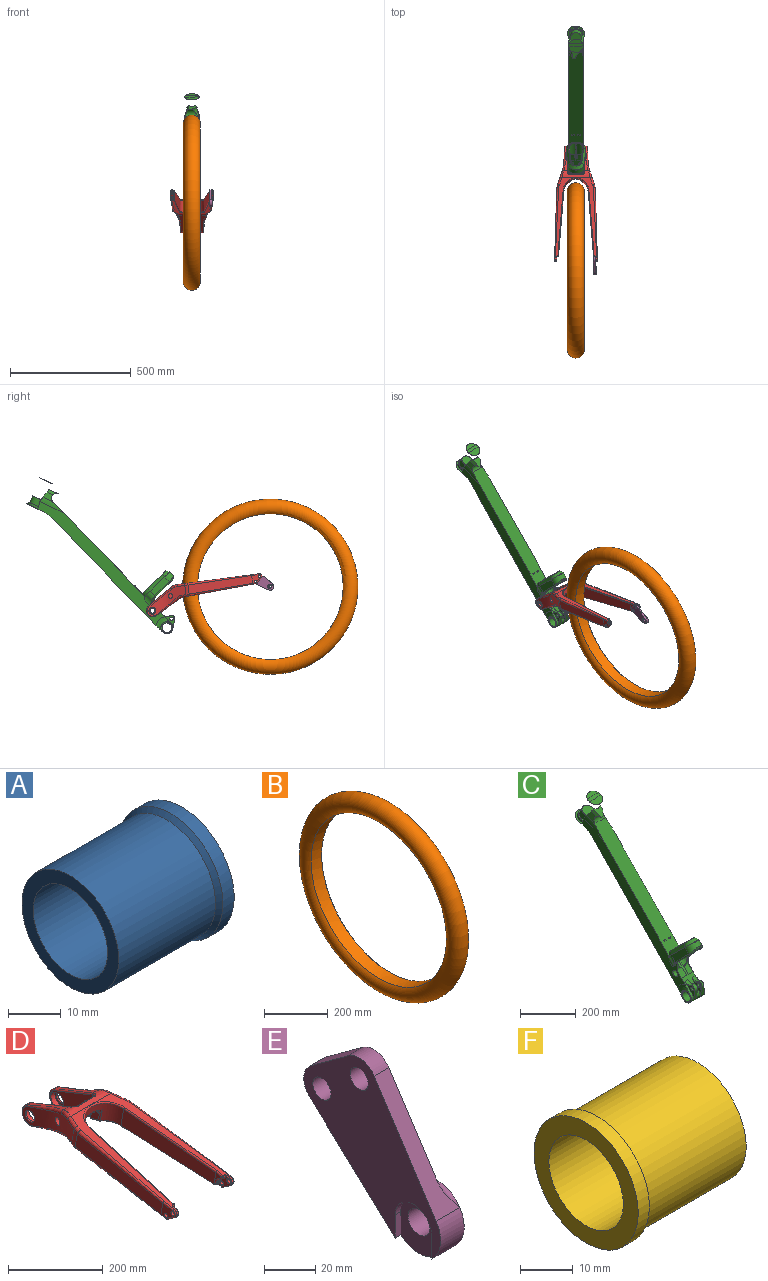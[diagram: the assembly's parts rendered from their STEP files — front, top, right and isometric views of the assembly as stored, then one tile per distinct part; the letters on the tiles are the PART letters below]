
ASSEMBLY  parts=6 mates=7
PART A: 6 faces, bbox 30x28x28 mm
  f0: cylinder r=13mm len=26mm, axis (-1,0,0), area 2123.7mm2, adj f3,f5
  f1: cylinder r=10mm len=30mm, axis (-1,0,0), area 1885mm2, adj f2,f3
  f2: plane 28x28mm, normal (1,0,0), area 301.6mm2, adj f1,f4
  f3: plane 26x26mm, normal (-1,0,0), area 216.8mm2, adj f0,f1
  f4: cylinder r=14mm len=28mm, axis (1,0,0), area 263.9mm2, adj f2,f5
  f5: cone r=14mm half-angle=45deg, axis (1,0,0), area 120mm2, adj f0,f4
PART B: 2 faces, bbox 47.1x784.7x784.7 mm
  f0: torus R=327.5mm, axis (-1,0,0), area 356678mm2, adj f1
  f1: cylinder r=301.59mm len=603.18mm, axis (1,0,0), area 89169.2mm2, adj f0
PART C: 127 faces, bbox 114.2x654.6x672 mm
  f0: cylinder r=14mm len=20.9mm, axis (-1,0,0), area 450.7mm2, adj f1,f2,f45,f63
  f1: plane 39.93x14mm, normal (0,-0.98,-0.21), area 572mm2, adj f0,f31,f45,f63
  f2: cylinder r=25mm len=30.24mm, axis (-1,0,0), area 460.2mm2, adj f0,f6,f45,f63
  f3: plane 13.6x6.41mm, normal (0,-0.9,-0.43), area 46.5mm2, adj f34,f53,f88,f90
  f4: cylinder r=27.5mm len=82.26mm, axis (0,0.7,0.72), area 2320.4mm2, adj f6,f18,f48,f105,f106,f108,f109
  f5: cylinder r=27.5mm len=93.75mm, axis (0,0.7,0.72), area 2418.2mm2, adj f6,f17,f52,f53,f56
  f6: plane 518.11x504.25mm, normal (0,-0.72,0.7), area 34991.8mm2, adj f2,f4,f5,f20,f22,f26,f31,f34
  f7: cylinder r=40.63mm len=44.38mm, axis (0,0.7,0.72), area 639mm2, adj f8,f26,f34,f88
  f8: cylinder r=40.5mm len=40.95mm, axis (0,0.7,0.72), area 751.8mm2, adj f7,f16,f26,f90,f92
  f9: cylinder r=40.63mm len=44.38mm, axis (0,0.7,0.72), area 639mm2, adj f10,f22,f35,f83
  f10: cylinder r=40.5mm len=40.95mm, axis (0,0.7,0.72), area 756.9mm2, adj f9,f19,f22,f87,f89,f91
  f11: cylinder r=14mm len=20.9mm, axis (-1,0,0), area 264.5mm2, adj f12,f57,f117,f118,f119,f125
  f12: plane 39.94x20.13mm, normal (0,-0.98,-0.21), area 591.2mm2, adj f11,f31,f115,f116,f124
  f13: cylinder r=19.5mm len=41.35mm, axis (0,0.7,0.72), area 2252mm2, adj f17,f18,f50,f100,f101,f102
  f14: cylinder r=32.5mm len=64.71mm, axis (0,0.7,0.72), area 2404.8mm2, adj f16,f19,f24,f69,f70,f97,f98,f99
  f15: plane 62.39x60.67mm, normal (0,-0.7,-0.72), area 665.4mm2, adj f17,f43,f53,f96,f98,f100
  f16: plane 79.78x78.67mm, normal (-1,-0.07,0.07), area 2352.5mm2, adj f8,f14,f25,f94,f96
  f17: plane 90.62x89.31mm, normal (1,0.07,-0.07), area 3668.3mm2, adj f5,f13,f15,f51,f53,f100
  f18: plane 88.63x87.78mm, normal (-1,0.07,-0.07), area 3427.2mm2, adj f4,f13,f49,f103,f104
  f19: plane 79.78x78.67mm, normal (1,-0.07,0.07), area 2352.5mm2, adj f10,f14,f23,f93,f95
  f20: plane 97.72x95.03mm, normal (0,0.7,0.72), area 490.3mm2, adj f6,f22,f23,f24,f25,f26,f48,f49
  f21: plane 62.39x60.67mm, normal (0,-0.7,-0.72), area 437.2mm2, adj f43,f54,f95,f97,f102,f103
  f22: bspline ~57.03x46.15mm, area 649.6mm2, adj f6,f9,f10,f20,f23,f35
  f23: bspline ~70.52x68mm, area 1360.7mm2, adj f19,f20,f22,f24
  f24: cone r=24.08mm half-angle=31.6deg, axis (0,-0.7,-0.72), area 1343.4mm2, adj f14,f20,f23,f25,f70
  f25: plane 70.52x68mm, normal (-0.85,0.31,0.43), area 1360.7mm2, adj f16,f20,f24,f26
  f26: cone r=32.08mm half-angle=31.6deg, axis (0,-0.7,-0.72), area 649.6mm2, adj f6,f7,f8,f20,f25,f34
  f27: plane 486.45x473.46mm, normal (0,0.72,-0.7), area 39699.1mm2, adj f31,f34,f35,f42,f46,f47
  f28: plane 70x63.93mm, normal (0,0.42,-0.91), area 1759.2mm2, adj f30,f34,f35,f42,f72
  f29: plane 60x54.38mm, normal (0,-0.42,0.91), area 2827.4mm2, adj f30
  f30: cone r=35mm half-angle=2.4deg, axis (0,0.42,-0.91), area 18673.1mm2, adj f28,f29,f34,f35,f36,f38,f39,f40
  f31: cylinder r=25mm len=68mm, axis (-1,0,0), area 4406.2mm2, adj f1,f6,f12,f27,f32,f33,f45,f63
  f32: plane 52.23x52.17mm, normal (1,0,0), area 703.6mm2, adj f31,f47,f59,f71,f115,f123
  f33: plane 50.04x50.04mm, normal (-1,0,0), area 706.9mm2, adj f31,f46,f71
  f34: plane 533.49x518.73mm, normal (-1,0,0), area 32458.6mm2, adj f3,f6,f7,f26,f27,f28,f30,f42
  f35: plane 532.73x520.81mm, normal (1,0,0), area 32191.3mm2, adj f6,f9,f22,f27,f28,f30,f40,f42
  f36: plane 38.13x32mm, normal (0,-0.42,0.91), area 954.4mm2, adj f30,f37,f38,f41,f44
  f37: cylinder r=20mm len=54.09mm, axis (-1,0,0), area 1926.3mm2, adj f6,f36,f41,f44,f80
  f38: plane 22.15x15.87mm, normal (0.91,-0.18,0.38), area 185.7mm2, adj f30,f36,f39,f44
  f39: plane 49.21x48.35mm, normal (0.98,-0.09,0.2), area 773.4mm2, adj f6,f30,f38,f40,f44
  f40: cylinder r=80mm len=97.39mm, axis (0,0.91,0.42), area 1320.5mm2, adj f6,f30,f35,f39
  f41: plane 48.89x23.35mm, normal (-0.91,-0.18,0.38), area 400.2mm2, adj f30,f36,f37,f80
  f42: bspline ~66x41.2mm, area 3061.4mm2, adj f27,f28,f34,f35
  f43: cylinder r=50mm len=53.79mm, axis (1,0,0), area 418.9mm2, adj f15,f21,f99,f101
  f44: bspline ~56.72x48.38mm, area 611.3mm2, adj f6,f36,f37,f38,f39
  f45: plane 59.4x51.14mm, normal (-1,0,0), area 840mm2, adj f0,f1,f2,f6,f31,f66
  f46: bspline ~84.75x83.82mm, area 1590.5mm2, adj f6,f27,f33,f34
  f47: bspline ~81.68x80.82mm, area 1515mm2, adj f27,f32,f35,f123
  f48: torus R=30.5mm, axis (0,0.7,0.72), area 182.5mm2, adj f4,f6,f20,f49
  f49: cylinder r=3mm len=62.3mm, axis (0.09,0.71,-0.69), area 398.8mm2, adj f18,f20,f48,f50
  f50: torus R=22.5mm, axis (0,0.7,0.72), area 286.5mm2, adj f13,f20,f49,f51
  f51: cylinder r=3mm len=62.3mm, axis (0.09,-0.71,0.69), area 398.8mm2, adj f17,f20,f50,f52
  f52: torus R=30.5mm, axis (0,0.7,0.72), area 182.5mm2, adj f5,f6,f20,f51
  f53: cylinder r=20mm len=8.23mm, axis (1,0,0), area 57.2mm2, adj f3,f5,f15,f17,f56,f92,f94
  f54: cylinder r=20mm len=5.6mm, axis (1,0,0), area 30.6mm2, adj f21,f86,f91,f93,f104,f106,f108
  f55: bspline ~57.54x28.6mm, area 859.5mm2, adj f6,f60,f105
  f56: bspline ~57.54x28.6mm, area 1118.3mm2, adj f5,f6,f34,f53
  f57: cylinder r=25mm len=30.24mm, axis (-1,0,0), area 408.3mm2, adj f6,f11,f62,f120,f126
  f58: bspline ~52.19x48.46mm, area 447.7mm2, adj f59,f112,f116,f117,f118,f119,f120,f122
  f59: torus R=53.89mm, axis (1,0,0), area 126.3mm2, adj f32,f58,f115,f123
  f60: bspline ~89.08x62.35mm, area 237.3mm2, adj f35,f55,f61,f85,f107
  f61: cylinder r=3mm len=13.08mm, axis (0,-0.7,-0.72), area 72.2mm2, adj f6,f35,f60,f62
  f62: torus R=28mm, axis (1,0,0), area 48.8mm2, adj f35,f57,f61,f121
  f63: plane 59.4x51.14mm, normal (1,0,0), area 840mm2, adj f0,f1,f2,f6,f31,f66
  f64: plane 41.65x39.35mm, normal (-1,0,0), area 576.3mm2, adj f6,f31,f65,f124,f125,f126
  f65: cylinder r=7mm len=14mm, axis (1,0,0), area 439.8mm2, adj f64,f113
  f66: cylinder r=7mm len=14mm, axis (1,0,0), area 615.8mm2, adj f45,f63
  f67: cylinder r=10mm len=7mm, axis (1,0,0), area 37.2mm2, adj f6,f77,f78,f111
  f68: cylinder r=10mm len=7mm, axis (1,0,0), area 37.2mm2, adj f6,f76,f79,f110
  f69: plane 7.62x1.13mm, normal (0,-0.26,0.97), area 2.4mm2, adj f14,f70
  f70: bspline ~13.36x2.85mm, area 28.4mm2, adj f14,f24,f69
  f71: cylinder r=20mm len=68mm, axis (1,0,0), area 8545.1mm2, adj f32,f33
  f72: cylinder r=27.75mm len=55.5mm, axis (0,0.42,-0.91), area 1743.6mm2, adj f28,f73
  f73: plane 55.5x50.3mm, normal (0,0.42,-0.91), area 757.3mm2, adj f72,f74
  f74: cylinder r=23mm len=54.37mm, axis (0,0.42,-0.91), area 4335.4mm2, adj f73,f75
  f75: plane 46x41.69mm, normal (0,0.42,-0.91), area 1661.9mm2, adj f74
  f76: torus R=12mm, axis (1,0,0), area 7mm2, adj f6,f68,f110
  f77: torus R=12mm, axis (1,0,0), area 7mm2, adj f6,f67,f111
  f78: torus R=12mm, axis (1,0,0), area 7mm2, adj f6,f67,f111
  f79: torus R=12mm, axis (1,0,0), area 7mm2, adj f6,f68,f110
  f80: plane 43.64x43.2mm, normal (-0.98,-0.09,0.2), area 870mm2, adj f6,f30,f37,f41,f81
  f81: cylinder r=100mm len=104.27mm, axis (0,0.91,0.42), area 1643.5mm2, adj f6,f30,f34,f80
  f82: cylinder r=13mm len=59mm, axis (1,0,0), area 4819.2mm2, adj f34,f114
  f83: bspline ~25.89x16.45mm, area 38.8mm2, adj f9,f84,f85,f87
  f84: bspline ~23.63x22.58mm, area 82.8mm2, adj f35,f83,f85
  f85: bspline ~24.54x10.4mm, area 114.3mm2, adj f60,f83,f84,f86,f87,f109
  f86: bspline ~14.83x11.3mm, area 36.8mm2, adj f54,f85,f89,f108
  f87: bspline ~10.79x9.47mm, area 44.9mm2, adj f10,f83,f85,f89
  f88: bspline ~22.11x14.75mm, area 104.7mm2, adj f3,f7,f34,f90
  f89: bspline ~13.75x9.79mm, area 50.7mm2, adj f10,f86,f87,f91
  f90: bspline ~20.07x13.73mm, area 127.4mm2, adj f3,f8,f88,f92
  f91: bspline ~12.99x11.67mm, area 63.4mm2, adj f10,f54,f89,f93
  f92: bspline ~12.99x11.67mm, area 65.4mm2, adj f8,f53,f90,f94
  f93: bspline ~9.31x9.09mm, area 2.5mm2, adj f19,f54,f91,f95
  f94: bspline ~9.31x9.09mm, area 2.5mm2, adj f16,f53,f92,f96
  f95: cylinder r=5mm len=63.3mm, axis (0.09,0.71,-0.69), area 661.7mm2, adj f19,f21,f93,f97
  f96: cylinder r=5mm len=63.3mm, axis (0.09,-0.71,0.69), area 661.7mm2, adj f15,f16,f94,f98
  f97: torus R=27.5mm, axis (0,-0.7,-0.72), area 27.9mm2, adj f14,f21,f95,f99
  f98: torus R=27.5mm, axis (0,-0.7,-0.72), area 27.9mm2, adj f14,f15,f96,f99
  f99: bspline ~64.48x28.28mm, area 562.7mm2, adj f14,f43,f97,f98
  f100: torus R=22.5mm, axis (0,-0.7,-0.72), area 41.8mm2, adj f13,f15,f17,f101
  f101: bspline ~44.49x16.77mm, area 292mm2, adj f13,f43,f100,f102
  f102: torus R=22.5mm, axis (0,-0.7,-0.72), area 15.8mm2, adj f13,f21,f101,f103
  f103: cylinder r=3mm len=62.09mm, axis (-0.09,-0.71,0.69), area 394.8mm2, adj f18,f21,f102,f104
  f104: bspline ~3.07x2.88mm, area 3.6mm2, adj f18,f54,f103,f106
  f105: bspline ~63.41x36.15mm, area 94.3mm2, adj f4,f6,f55,f107
  f106: bspline ~8.04x7.27mm, area 22.3mm2, adj f4,f54,f104,f108
  f107: sphere r=3mm, area 1.6mm2, adj f60,f105,f109
  f108: bspline ~17.24x6.16mm, area 58.8mm2, adj f4,f54,f86,f106,f109
  f109: bspline ~5.05x4.73mm, area 10.9mm2, adj f4,f85,f107,f108
  f110: plane 10.94x1.43mm, normal (0,0.41,0.91), area 14.4mm2, adj f6,f68,f76,f79
  f111: plane 10.94x1.43mm, normal (0,0.41,0.91), area 14.4mm2, adj f6,f67,f77,f78
  f112: cylinder r=9mm len=18mm, axis (-1,0,0), area 351.2mm2, adj f58,f113
  f113: plane 18x18mm, normal (1,0,0), area 100.5mm2, adj f65,f112
  f114: cone r=13mm half-angle=45deg, axis (1,0,0), area 120mm2, adj f35,f82
  f115: bspline ~57.42x14.42mm, area 126.3mm2, adj f12,f31,f32,f59,f116
  f116: bspline ~18.75x6.05mm, area 33.3mm2, adj f12,f58,f115,f117
  f117: bspline ~12.15x4.15mm, area 37.9mm2, adj f11,f58,f116,f118
  f118: bspline ~12.38x10.16mm, area 59.9mm2, adj f11,f58,f117,f119
  f119: bspline ~11.71x5.17mm, area 35.7mm2, adj f11,f58,f118,f120
  f120: bspline ~28.61x9.38mm, area 94.4mm2, adj f57,f58,f119,f121
  f121: sphere r=3mm, area 1.5mm2, adj f62,f120,f122
  f122: bspline ~3.08x3.06mm, area 0.9mm2, adj f35,f58,f121,f123
  f123: bspline ~34.16x33.28mm, area 48.3mm2, adj f32,f47,f58,f59,f122
  f124: cylinder r=3mm len=40.56mm, axis (0,0.21,-0.98), area 164.5mm2, adj f12,f31,f64,f125
  f125: torus R=11mm, axis (1,0,0), area 139.9mm2, adj f11,f64,f124,f126
  f126: torus R=28mm, axis (1,0,0), area 132.3mm2, adj f6,f57,f64,f125
PART D: 203 faces, bbox 197.4x507.1x157.3 mm
  f0: cylinder r=14mm len=28mm, axis (1,0,0), area 356.6mm2, adj f47,f196
  f1: bspline ~192.5x24.16mm, area 734.9mm2, adj f2,f41,f89,f156,f158,f160
  f2: plane 113.85x38.88mm, normal (0,-0.31,-0.95), area 1516.8mm2, adj f1,f40,f91,f136,f137,f154
  f3: cylinder r=5mm len=10mm, axis (-1,0,0), area 235.6mm2, adj f9,f125
  f4: cylinder r=5mm len=10mm, axis (-1,0,0), area 235.6mm2, adj f9,f126
  f5: cylinder r=10mm len=7.21mm, axis (-1,0,0), area 31.9mm2, adj f6,f15,f61,f119
  f6: plane 24.07x18.55mm, normal (0,-0.59,-0.81), area 109.1mm2, adj f5,f7,f59,f117
  f7: cylinder r=10mm len=17.91mm, axis (-1,0,0), area 102.6mm2, adj f6,f10,f57,f115
  f8: bspline ~192.5x30.61mm, area 2259mm2, adj f10,f11,f39,f66,f84,f140,f141,f142
  f9: plane 44.65x36.76mm, normal (1,0,0), area 812.8mm2, adj f3,f4,f17,f57,f58,f59,f61,f63
  f10: plane 336.07x171.54mm, normal (0,-0.18,0.98), area 11180.5mm2, adj f7,f8,f29,f37,f53,f58,f60,f62
  f11: plane 112.04x45.23mm, normal (0,0.37,0.93), area 1157.6mm2, adj f8,f12,f68,f145
  f12: cylinder r=25mm len=48.18mm, axis (-1,0,0), area 770.3mm2, adj f11,f14,f70,f72,f74,f146
  f13: bspline ~192.5x24.16mm, area 735.1mm2, adj f14,f15,f71,f155,f157,f159
  f14: plane 113.86x38.89mm, normal (0,-0.31,-0.95), area 1516.8mm2, adj f12,f13,f73,f147,f148,f153
  f15: plane 301.16x44.4mm, normal (0,0.13,-0.99), area 4615.2mm2, adj f5,f13,f32,f63,f65,f67,f69,f121
  f16: cylinder r=80.54mm len=40.19mm, axis (0,-0.18,0.98), area 534.9mm2, adj f17,f23,f62,f67
  f17: plane 269.48x76.04mm, normal (1,0.03,0.01), area 9636.1mm2, adj f9,f16,f60,f65,f67
  f18: plane 32.81x23.88mm, normal (-1,0,0), area 220.5mm2, adj f19,f165,f169,f173,f175,f179,f183
  f19: plane 262.75x79.78mm, normal (-1,-0.08,-0.01), area 10375.8mm2, adj f18,f20,f163,f165,f185
  f20: cylinder r=50mm len=99.67mm, axis (0,-0.18,0.98), area 5472.5mm2, adj f19,f45,f133,f134,f135,f159,f160,f161
  f21: plane 46.59x25.52mm, normal (0,0.98,0.18), area 1052.4mm2, adj f128,f129,f131,f142,f188,f192
  f22: plane 127.61x88.35mm, normal (-1,0,0), area 4462.8mm2, adj f129,f144,f145,f146,f147,f198,f200
  f23: bspline ~189.88x153.73mm, area 7194.3mm2, adj f16,f64,f66,f68,f69,f70,f71,f72
  f24: cylinder r=10mm len=10.98mm, axis (-1,0,0), area 49.4mm2, adj f25,f31,f118,f173
  f25: plane 16.79x12.28mm, normal (0,-0.59,-0.81), area 83.2mm2, adj f24,f30,f116,f175
  f26: plane 39.88x34.63mm, normal (-1,0,0), area 513.8mm2, adj f110,f112,f113,f114,f115,f116,f117,f118
  f27: plane 4x1.5mm, normal (0,-0.81,-0.59), area 7.4mm2, adj f31,f32,f122,f169
  f28: plane 4x1.52mm, normal (0,-0.98,0.22), area 6.3mm2, adj f29,f30,f112,f179
  f29: cylinder r=3mm len=4mm, axis (-1,0,0), area 14mm2, adj f10,f28,f110,f181
  f30: cylinder r=3mm len=4mm, axis (1,0,0), area 14mm2, adj f25,f28,f114,f177
  f31: cylinder r=3mm len=4mm, axis (-1,0,0), area 11.1mm2, adj f24,f27,f120,f171
  f32: cylinder r=3mm len=4mm, axis (1,0,0), area 12.8mm2, adj f15,f27,f124,f167
  f33: cylinder r=5mm len=10mm, axis (1,0,0), area 235.6mm2, adj f38,f108
  f34: cylinder r=5mm len=10mm, axis (1,0,0), area 235.6mm2, adj f38,f109
  f35: cylinder r=10mm len=7.21mm, axis (1,0,0), area 31.9mm2, adj f36,f41,f79,f98
  f36: plane 21.53x16.02mm, normal (0,-0.59,-0.81), area 109.1mm2, adj f35,f37,f77,f96
  f37: cylinder r=10mm len=17.91mm, axis (1,0,0), area 102.6mm2, adj f10,f36,f75,f94
  f38: plane 45.68x37.79mm, normal (-1,0,0), area 812.8mm2, adj f33,f34,f43,f75,f76,f77,f79,f81
  f39: plane 112.04x45.23mm, normal (0,0.37,0.93), area 1157.9mm2, adj f8,f40,f86,f139
  f40: cylinder r=25mm len=48.18mm, axis (1,0,0), area 770.3mm2, adj f2,f39,f88,f90,f92,f138
  f41: plane 301.16x44.4mm, normal (0,0.13,-0.99), area 4616.4mm2, adj f1,f35,f56,f81,f83,f85,f87,f100
  f42: cylinder r=80.54mm len=40.19mm, axis (0,-0.18,0.98), area 535mm2, adj f43,f47,f80,f85
  f43: plane 269.48x76.04mm, normal (-1,0.03,0.01), area 9632.8mm2, adj f38,f42,f78,f83,f85
  f44: plane 32.81x23.88mm, normal (1,0,0), area 220.5mm2, adj f45,f166,f170,f174,f176,f180,f184
  f45: plane 262.75x79.78mm, normal (1,-0.08,-0.01), area 10375.8mm2, adj f20,f44,f164,f166,f186
  f46: plane 127.61x88.35mm, normal (1,0,0), area 4462.8mm2, adj f128,f137,f138,f139,f140,f197,f202
  f47: bspline ~189.88x153.73mm, area 6930.1mm2, adj f0,f42,f82,f84,f86,f87,f88,f89
  f48: cylinder r=10mm len=10.98mm, axis (1,0,0), area 49.4mm2, adj f49,f55,f105,f174
  f49: plane 16.79x12.28mm, normal (0,-0.59,-0.81), area 83.2mm2, adj f48,f54,f103,f176
  f50: plane 39.88x34.63mm, normal (1,0,0), area 513.8mm2, adj f93,f94,f96,f97,f98,f99,f100,f101
  f51: plane 4x1.5mm, normal (0,-0.81,-0.59), area 7.4mm2, adj f55,f56,f106,f170
  f52: plane 4x1.52mm, normal (0,-0.98,0.22), area 6.3mm2, adj f53,f54,f99,f180
  f53: cylinder r=3mm len=4mm, axis (1,0,0), area 14mm2, adj f10,f52,f97,f182
  f54: cylinder r=3mm len=4mm, axis (-1,0,0), area 14mm2, adj f49,f52,f101,f178
  f55: cylinder r=3mm len=4mm, axis (1,0,0), area 11.1mm2, adj f48,f51,f107,f172
  f56: cylinder r=3mm len=4mm, axis (-1,0,0), area 12.8mm2, adj f41,f51,f104,f168
  f57: bspline ~17.91x8.91mm, area 100.2mm2, adj f7,f9,f58,f59
  f58: bspline ~31.05x8.65mm, area 146.8mm2, adj f9,f10,f57,f60
  f59: bspline ~22.46x17.53mm, area 128.1mm2, adj f6,f9,f57,f61
  f60: bspline ~289.38x56.3mm, area 1995.6mm2, adj f10,f17,f58,f62
  f61: bspline ~7.21x4.59mm, area 34.9mm2, adj f5,f9,f59,f63
  f62: bspline ~16.63x10.94mm, area 167mm2, adj f10,f16,f60,f64
  f63: bspline ~15.08x5.36mm, area 74.3mm2, adj f9,f15,f61,f65
  f64: bspline ~104.64x41.39mm, area 408mm2, adj f10,f23,f62,f66
  f65: bspline ~285.74x45.17mm, area 2184mm2, adj f15,f17,f63,f67
  f66: bspline ~33.81x16.04mm, area 366.1mm2, adj f8,f23,f64,f68
  f67: bspline ~15.29x10.66mm, area 160.8mm2, adj f15,f16,f17,f65,f69
  f68: bspline ~112.79x48.01mm, area 997.7mm2, adj f11,f23,f66,f70
  f69: bspline ~13.76x11.34mm, area 148.1mm2, adj f15,f23,f67,f71
  f70: bspline ~16.83x14.04mm, area 74.9mm2, adj f12,f23,f68,f72
  f71: bspline ~29.02x16.44mm, area 358mm2, adj f13,f23,f69,f73
  f72: bspline ~20.52x6.73mm, area 76.3mm2, adj f12,f23,f70,f74
  f73: bspline ~111.94x44.07mm, area 1053mm2, adj f14,f23,f71,f74
  f74: bspline ~35.89x23.14mm, area 194.8mm2, adj f12,f23,f72,f73
  f75: bspline ~17.91x8.91mm, area 100.2mm2, adj f37,f38,f76,f77
  f76: bspline ~32.57x8.93mm, area 146.8mm2, adj f10,f38,f75,f78
  f77: bspline ~22.46x17.53mm, area 128.1mm2, adj f36,f38,f75,f79
  f78: bspline ~289.38x56.3mm, area 1995.8mm2, adj f10,f43,f76,f80
  f79: bspline ~7.21x4.59mm, area 34.9mm2, adj f35,f38,f77,f81
  f80: bspline ~16.63x10.94mm, area 167mm2, adj f10,f42,f78,f82
  f81: bspline ~15.08x5.36mm, area 74.3mm2, adj f38,f41,f79,f83
  f82: bspline ~104.64x41.39mm, area 408mm2, adj f10,f47,f80,f84
  f83: bspline ~285.74x45.17mm, area 2183.8mm2, adj f41,f43,f81,f85
  f84: bspline ~33.81x16.04mm, area 366mm2, adj f8,f47,f82,f86
  f85: bspline ~15.29x10.66mm, area 160.8mm2, adj f41,f42,f43,f83,f87
  f86: bspline ~112.79x48.01mm, area 997.7mm2, adj f39,f47,f84,f88
  f87: bspline ~13.76x11.34mm, area 148.1mm2, adj f41,f47,f85,f89
  f88: bspline ~16.83x14.04mm, area 74.9mm2, adj f40,f47,f86,f90
  f89: bspline ~29.02x16.44mm, area 358mm2, adj f1,f47,f87,f91
  f90: bspline ~20.52x6.73mm, area 76.3mm2, adj f40,f47,f88,f92
  f91: bspline ~111.94x44.07mm, area 1053.1mm2, adj f2,f47,f89,f92
  f92: bspline ~35.89x23.14mm, area 194.8mm2, adj f40,f47,f90,f91
  f93: cylinder r=1mm len=9.8mm, axis (0,-0.98,-0.18), area 15.4mm2, adj f10,f50,f94,f95
  f94: torus R=9mm, axis (1,0,0), area 35.2mm2, adj f37,f50,f93,f96
  f95: bspline ~3.54x2mm, area 1.9mm2, adj f10,f93,f97
  f96: cylinder r=1mm len=21.11mm, axis (0,0.81,-0.59), area 39.9mm2, adj f36,f50,f94,f98
  f97: torus R=4mm, axis (1,0,0), area 2.7mm2, adj f50,f53,f95,f99
  f98: torus R=9mm, axis (1,0,0), area 11.5mm2, adj f35,f50,f96,f100
  f99: cylinder r=1mm len=1.75mm, axis (0,-0.22,-0.98), area 2.5mm2, adj f50,f52,f97,f101
  f100: cylinder r=1mm len=9.32mm, axis (0,0.99,0.13), area 14.6mm2, adj f41,f50,f98,f102
  f101: torus R=4mm, axis (1,0,0), area 6.1mm2, adj f50,f54,f99,f103
  f102: bspline ~3.97x2mm, area 2mm2, adj f41,f100,f104
  f103: cylinder r=1mm len=17.38mm, axis (0,0.81,-0.59), area 32.7mm2, adj f49,f50,f101,f105
  f104: torus R=4mm, axis (1,0,0), area 2.2mm2, adj f50,f56,f102,f106
  f105: torus R=9mm, axis (1,0,0), area 18.7mm2, adj f48,f50,f103,f107
  f106: cylinder r=1mm len=2.09mm, axis (0,0.59,-0.81), area 2.9mm2, adj f50,f51,f104,f107
  f107: torus R=4mm, axis (1,0,0), area 4.9mm2, adj f50,f55,f105,f106
  f108: torus R=6mm, axis (1,0,0), area 52.9mm2, adj f33,f50
  f109: torus R=6mm, axis (1,0,0), area 52.9mm2, adj f34,f50
  f110: torus R=4mm, axis (-1,0,0), area 2.7mm2, adj f26,f29,f111,f112
  f111: bspline ~3.54x2mm, area 1.9mm2, adj f10,f110,f113
  f112: cylinder r=1mm len=1.75mm, axis (0,-0.22,-0.98), area 2.5mm2, adj f26,f28,f110,f114
  f113: cylinder r=1mm len=9.8mm, axis (0,-0.98,-0.18), area 15.4mm2, adj f10,f26,f111,f115
  f114: torus R=4mm, axis (-1,0,0), area 6.1mm2, adj f26,f30,f112,f116
  f115: torus R=9mm, axis (-1,0,0), area 35.2mm2, adj f7,f26,f113,f117
  f116: cylinder r=1mm len=17.38mm, axis (0,0.81,-0.59), area 32.7mm2, adj f25,f26,f114,f118
  f117: cylinder r=1mm len=21.11mm, axis (0,0.81,-0.59), area 39.9mm2, adj f6,f26,f115,f119
  f118: torus R=9mm, axis (-1,0,0), area 18.7mm2, adj f24,f26,f116,f120
  f119: torus R=9mm, axis (-1,0,0), area 11.5mm2, adj f5,f26,f117,f121
  f120: torus R=4mm, axis (-1,0,0), area 4.9mm2, adj f26,f31,f118,f122
  f121: cylinder r=1mm len=9.32mm, axis (0,0.99,0.13), area 14.6mm2, adj f15,f26,f119,f123
  f122: cylinder r=1mm len=2.09mm, axis (0,0.59,-0.81), area 2.9mm2, adj f26,f27,f120,f124
  f123: bspline ~3.97x2mm, area 2mm2, adj f15,f121,f124
  f124: torus R=4mm, axis (-1,0,0), area 2.2mm2, adj f26,f32,f122,f123
  f125: torus R=6mm, axis (-1,0,0), area 52.9mm2, adj f3,f26
  f126: torus R=6mm, axis (-1,0,0), area 52.9mm2, adj f4,f26
  f127: cylinder r=14mm len=28mm, axis (-1,0,0), area 354.7mm2, adj f23,f199
  f128: cylinder r=10mm len=66.76mm, axis (0,-0.18,0.98), area 813.1mm2, adj f21,f46,f136,f141,f150,f192
  f129: cylinder r=10mm len=66.76mm, axis (0,-0.18,0.98), area 813.1mm2, adj f21,f22,f143,f148,f149,f188
  f130: plane 28.29x26.52mm, normal (1,0,0), area 497.5mm2, adj f135,f150,f154,f156,f193,f194
  f131: plane 33.44x17.24mm, normal (0,0.18,-0.98), area 522.9mm2, adj f21,f134,f188,f189,f192,f193
  f132: plane 28.29x26.52mm, normal (-1,0,0), area 497.5mm2, adj f133,f149,f153,f155,f189,f190
  f133: cylinder r=5mm len=31.55mm, axis (0,-0.18,0.98), area 127mm2, adj f20,f132,f157,f191
  f134: torus R=55mm, axis (0,-0.18,0.98), area 336.6mm2, adj f20,f131,f190,f191,f194,f195
  f135: cylinder r=5mm len=31.55mm, axis (0,-0.18,0.98), area 127mm2, adj f20,f130,f158,f195
  f136: bspline ~15.16x11.4mm, area 81.1mm2, adj f2,f128,f137,f152
  f137: cylinder r=3mm len=88.86mm, axis (0,0.95,-0.31), area 435.7mm2, adj f2,f46,f136,f138
  f138: torus R=22mm, axis (-1,0,0), area 346.1mm2, adj f40,f46,f137,f139
  f139: cylinder r=3mm len=113.17mm, axis (0,-0.93,0.37), area 569.4mm2, adj f39,f46,f138,f140
  f140: bspline ~8.33x5.68mm, area 9.2mm2, adj f8,f46,f139,f141
  f141: bspline ~17.05x14.41mm, area 80.3mm2, adj f8,f128,f140,f142
  f142: cylinder r=3mm len=46mm, axis (1,0,0), area 188.3mm2, adj f8,f21,f141,f143
  f143: bspline ~17.05x14.41mm, area 80.3mm2, adj f8,f129,f142,f144
  f144: bspline ~8.33x5.68mm, area 9.2mm2, adj f8,f22,f143,f145
  f145: cylinder r=3mm len=113.17mm, axis (0,-0.93,0.37), area 569.4mm2, adj f11,f22,f144,f146
  f146: torus R=22mm, axis (1,0,0), area 346.1mm2, adj f12,f22,f145,f147
  f147: cylinder r=3mm len=88.86mm, axis (0,0.95,-0.31), area 435.7mm2, adj f14,f22,f146,f148
  f148: bspline ~15.16x11.4mm, area 81.1mm2, adj f14,f129,f147,f151
  f149: cylinder r=3mm len=28.81mm, axis (0,-0.18,0.98), area 105.1mm2, adj f129,f132,f151,f188
  f150: cylinder r=3mm len=28.81mm, axis (0,-0.18,0.98), area 105.1mm2, adj f128,f130,f152,f192
  f151: sphere r=3mm, area 8.7mm2, adj f148,f149,f153
  f152: sphere r=3mm, area 9.7mm2, adj f136,f150,f154
  f153: cylinder r=3mm len=10.79mm, axis (0,0.95,-0.31), area 48.9mm2, adj f14,f132,f151,f155
  f154: cylinder r=3mm len=10.79mm, axis (0,-0.95,0.31), area 48.9mm2, adj f2,f130,f152,f156
  f155: bspline ~29x10.35mm, area 61.4mm2, adj f13,f132,f153,f157
  f156: bspline ~29.19x10.41mm, area 61.4mm2, adj f1,f130,f154,f158
  f157: bspline ~5.87x4.4mm, area 16.7mm2, adj f13,f133,f155,f159
  f158: bspline ~5.53x4.1mm, area 16.7mm2, adj f1,f135,f156,f160
  f159: bspline ~17.13x15.02mm, area 69.7mm2, adj f13,f20,f157,f161
  f160: bspline ~17.13x15.02mm, area 69.7mm2, adj f1,f20,f158,f162
  f161: bspline ~30.16x14.52mm, area 146.8mm2, adj f15,f20,f159,f163
  f162: bspline ~30.16x14.52mm, area 146.8mm2, adj f20,f41,f160,f164
  f163: cylinder r=3mm len=257.44mm, axis (-0.08,0.99,0.13), area 1221.1mm2, adj f15,f19,f161,f165
  f164: cylinder r=3mm len=257.44mm, axis (0.08,0.99,0.13), area 1221.1mm2, adj f41,f45,f162,f166
  f165: cylinder r=3mm len=3.15mm, axis (0,0.99,0.13), area 6mm2, adj f15,f18,f19,f163,f167
  f166: cylinder r=3mm len=3.15mm, axis (0,0.99,0.13), area 6mm2, adj f41,f44,f45,f164,f168
  f167: sphere r=3mm, area 9.6mm2, adj f32,f165,f169
  f168: sphere r=3mm, area 9.6mm2, adj f56,f166,f170
  f169: cylinder r=3mm len=3.52mm, axis (0,0.59,-0.81), area 8.8mm2, adj f18,f27,f167,f171
  f170: cylinder r=3mm len=3.52mm, axis (0,0.59,-0.81), area 8.8mm2, adj f44,f51,f168,f172
  f171: sphere r=3mm, area 8.3mm2, adj f31,f169,f173
  f172: sphere r=3mm, area 11.4mm2, adj f55,f170,f174
  f173: torus R=13mm, axis (-1,0,0), area 64.5mm2, adj f18,f24,f171,f175
  f174: torus R=13mm, axis (1,0,0), area 64.5mm2, adj f44,f48,f172,f176
  f175: cylinder r=3mm len=18.56mm, axis (0,-0.81,0.59), area 98mm2, adj f18,f25,f173,f177
  f176: cylinder r=3mm len=18.56mm, axis (0,-0.81,0.59), area 98mm2, adj f44,f49,f174,f178
  f177: sphere r=3mm, area 10.5mm2, adj f30,f175,f179
  f178: sphere r=3mm, area 10.5mm2, adj f54,f176,f180
  f179: cylinder r=3mm len=3.27mm, axis (0,-0.22,-0.98), area 7.4mm2, adj f18,f28,f177,f181
  f180: cylinder r=3mm len=3.27mm, axis (0,-0.22,-0.98), area 7.4mm2, adj f44,f52,f178,f182
  f181: sphere r=3mm, area 6.7mm2, adj f29,f179,f183
  f182: sphere r=3mm, area 10.5mm2, adj f53,f180,f184
  f183: cylinder r=3mm len=18.15mm, axis (0,-0.98,-0.18), area 84.1mm2, adj f10,f18,f181,f185
  f184: cylinder r=3mm len=18.15mm, axis (0,-0.98,-0.18), area 84.1mm2, adj f10,f44,f182,f186
  f185: cylinder r=3mm len=254.7mm, axis (0.08,-0.98,-0.18), area 1222.8mm2, adj f10,f19,f183,f187
  f186: cylinder r=3mm len=254.7mm, axis (-0.08,-0.98,-0.18), area 1222.8mm2, adj f10,f45,f184,f187
  f187: torus R=53mm, axis (0,-0.18,0.98), area 717mm2, adj f10,f20,f185,f186
  f188: torus R=11mm, axis (0,-0.18,0.98), area 33.5mm2, adj f21,f129,f131,f149,f189
  f189: cylinder r=8mm len=16.54mm, axis (0,-0.98,-0.18), area 192.7mm2, adj f131,f132,f188,f190
  f190: bspline ~9.21x8.52mm, area 49.1mm2, adj f132,f134,f189,f191
  f191: bspline ~11.33x9.42mm, area 36.3mm2, adj f133,f134,f190
  f192: torus R=11mm, axis (0,-0.18,0.98), area 33.5mm2, adj f21,f128,f131,f150,f193
  f193: cylinder r=8mm len=16.54mm, axis (0,0.98,0.18), area 192.7mm2, adj f130,f131,f192,f194
  f194: bspline ~9.21x8.52mm, area 49.1mm2, adj f130,f134,f193,f195
  f195: bspline ~11.33x9.42mm, area 36.3mm2, adj f134,f135,f194
  f196: plane 38x38mm, normal (1,0,0), area 518.4mm2, adj f0,f197
  f197: cylinder r=19mm len=38mm, axis (1,0,0), area 1432.6mm2, adj f46,f196
  f198: cylinder r=19mm len=38mm, axis (1,0,0), area 1432.6mm2, adj f22,f199
  f199: plane 38x38mm, normal (-1,0,0), area 518.4mm2, adj f127,f198
  f200: cylinder r=9mm len=18mm, axis (-1,0,0), area 961.3mm2, adj f22,f201
  f201: plane 18x18mm, normal (-1,0,0), area 254.5mm2, adj f200
  f202: cylinder r=9mm len=23.61mm, axis (1,0,0), area 1335.3mm2, adj f46,f47
PART E: 17 faces, bbox 16.6x81.8x83.7 mm
  f0: plane 76.18x75.52mm, normal (-1,0,0), area 2532mm2, adj f1,f2,f3,f4,f7,f8,f9,f10
  f1: cylinder r=10mm len=15.41mm, axis (1,0,0), area 141mm2, adj f0,f2,f4,f5
  f2: plane 20.52x15mm, normal (0,0.59,0.81), area 203.3mm2, adj f0,f1,f3,f5
  f3: cylinder r=10mm len=14.27mm, axis (1,0,0), area 129.8mm2, adj f0,f2,f5,f7
  f4: plane 47.12x43.67mm, normal (0,0.68,-0.73), area 538.5mm2, adj f0,f1,f5,f8,f12
  f5: plane 67.01x65.83mm, normal (1,0,0), area 2052.7mm2, adj f1,f2,f3,f4,f7,f9,f10,f12
  f6: cylinder r=6mm len=12mm, axis (1,0,0), area 377mm2, adj f11,f16
  f7: plane 52.26x34.18mm, normal (0,-0.84,0.55), area 524.2mm2, adj f0,f3,f5,f8,f12
  f8: cylinder r=15mm len=25.2mm, axis (1,0,0), area 499.3mm2, adj f0,f4,f7,f11,f14,f15,f16
  f9: cylinder r=5mm len=10mm, axis (1,0,0), area 251.3mm2, adj f0,f5
  f10: cylinder r=5mm len=10mm, axis (1,0,0), area 251.3mm2, adj f0,f5
  f11: plane 30x30mm, normal (1,0,0), area 593.8mm2, adj f6,f8,f12
  f12: torus R=20mm, axis (-1,0,0), area 335.8mm2, adj f4,f5,f7,f11
  f13: cylinder r=10mm len=20mm, axis (-1,0,0), area 94.2mm2, adj f0,f14,f15,f16
  f14: plane 11.18x3mm, normal (0,1,0), area 33.5mm2, adj f0,f8,f13,f16
  f15: plane 11.18x3mm, normal (0,-1,0), area 33.5mm2, adj f0,f8,f13,f16
  f16: plane 25x20mm, normal (-1,0,0), area 320mm2, adj f6,f8,f13,f14,f15
PART F: 6 faces, bbox 30x28x28 mm
  f0: cylinder r=13mm len=27mm, axis (1,0,0), area 2205.4mm2, adj f3,f4
  f1: cylinder r=10mm len=30mm, axis (1,0,0), area 1885mm2, adj f2,f3
  f2: plane 28x28mm, normal (-1,0,0), area 301.6mm2, adj f1,f5
  f3: plane 26x26mm, normal (1,0,0), area 216.8mm2, adj f0,f1
  f4: plane 28x28mm, normal (1,0,0), area 84.8mm2, adj f0,f5
  f5: cylinder r=14mm len=28mm, axis (-1,0,0), area 263.9mm2, adj f2,f4
PLACE A at identity
PLACE B rot(axis=(-1,0,0),16.6deg) t=(-1.07,-15.25,31.67)mm
PLACE C at identity fixed
PLACE D rot(axis=(-1,0,0),18deg) t=(0,-18.66,21.91)mm
PLACE E rot(axis=(-1,0,0),18deg) t=(0,-18.66,21.91)mm
PLACE F at identity
MATE cylindrical D.f115 <-> E.f3  axis (-1,0,0) through (83.75,-382.4,213.19)mm
MATE cylindrical E.f6 <-> B.f0  axis (1,0,0) through (79,-427.9,170.12)mm
MATE cylindrical E.f1 <-> D.f98  axis (1,0,0) through (75,-367.51,192.6)mm
MATE planar D.f22 <-> A.f4  axis (-1,0,0) through (33,16.91,105.34)mm
MATE cylindrical C.f82 <-> A.f5  axis (1,0,0) through (-0.5,60,70)mm
MATE planar E.f5 <-> D.f26  axis (1,0,0) through (79,-390.11,193.35)mm
MATE planar F.f0 <-> C.f34  axis (1,0,0) through (-30,60,70)mm
